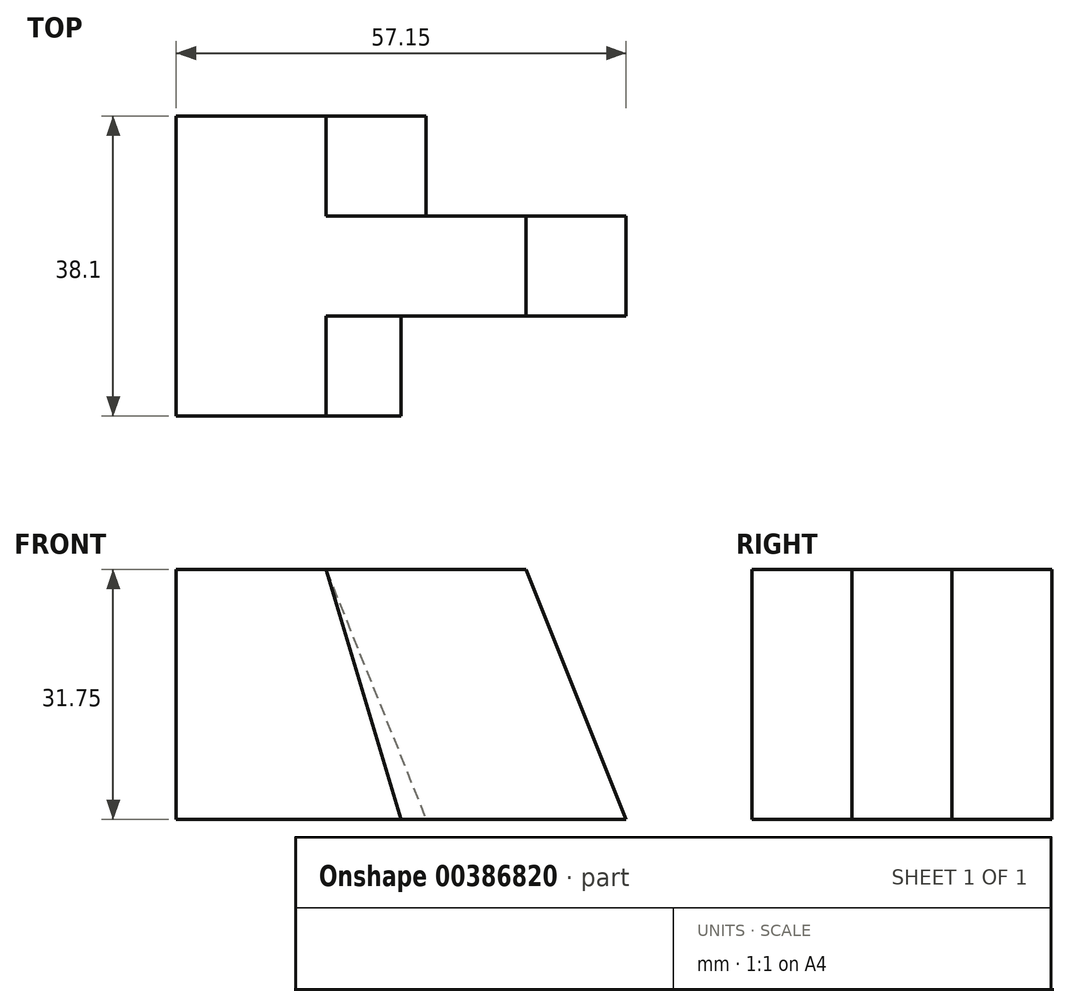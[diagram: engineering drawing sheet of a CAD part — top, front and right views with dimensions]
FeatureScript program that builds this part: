
annotation { "Feature Type Name" : "Feature", "Feature Type Description" : "" }
export const myFeature = defineFeature(function(context is Context, id is Id, definition is map)
    precondition{}
    {
        {
            var Q0;
            Q0=qCreatedBy(makeId("Front.planeOp"),FACE);
            var sketch = newSketch(context, id + "F0", { "sketchPlane" : qUnion([Q0])});
            skLineSegment(sketch, "E0", {"start": v(0, 0) * mm, "end": v(31.75, 0) * mm});
            skLineSegment(sketch, "E1", {"start": v(0, 0) * mm, "end": v(0, 31.75) * mm});
            skLineSegment(sketch, "E2", {"start": v(0, 31.75) * mm, "end": v(19.05, 31.75) * mm});
            skLineSegment(sketch, "E3", {"start": v(19.05, 31.75) * mm, "end": v(31.75, 0) * mm});
            skSolve(sketch);
        }
        {
            var Q0;
            Q0=makeQuery(id+"F0.imprint","IMPRINT",FACE,{"disambiguationData":[TD([[makeQuery(id+"F0.imprint","IMPRINT",EDGE,{"derivedFrom":sQuery(id+"F0.wireOp",EDGE,"E0")}),1.0]])]});
            extrude(context, id + "F1", {"entities" : qUnion([Q0]), "depth" : 25.4 * mm});
        }
        {
            var Q0;
            Q0=makeQuery(id+"F1.opExtrude","CAP_FACE",FACE,{"disambiguationData":[OSD([sQuery(id+"F0.wireOp",EDGE,"E0"),sQuery(id+"F0.wireOp",EDGE,"E1"),sQuery(id+"F0.wireOp",EDGE,"E2"),sQuery(id+"F0.wireOp",EDGE,"E3")])],"isStart":false});
            var sketch = newSketch(context, id + "F2", { "sketchPlane" : qUnion([Q0])});
            skLineSegment(sketch, "E4", {"start": v(31.75, 0) * mm, "end": v(57.15, 0) * mm});
            skLineSegment(sketch, "E5", {"start": v(19.05, 31.75) * mm, "end": v(44.45, 31.75) * mm});
            skLineSegment(sketch, "E6", {"start": v(44.45, 31.75) * mm, "end": v(57.15, 0) * mm});
            skSolve(sketch);
        }
        {
            var Q0;
            Q0=makeQuery(id+"F2.imprint","IMPRINT",FACE,{"disambiguationData":[TD([[makeQuery(id+"F2.imprint","IMPRINT",EDGE,{"derivedFrom":sQuery(id+"F2.wireOp",EDGE,"E4")}),1.0]])]});
            extrude(context, id + "F3", {"entities" : qUnion([Q0]), "operationType" : NewBodyOperationType.ADD, "oppositeDirection" : true, "depth" : 12.7 * mm});
        }
        {
            var Q0;
            {var subQ0=sQuery(id+"F0.wireOp",EDGE,"E3");Q0=makeQuery(id+"F3.boolean.opBoolean","MERGE",FACE,{"derivedFrom":[makeQuery(id+"F1.opExtrude","CAP_FACE",FACE,{"disambiguationData":[OSD([sQuery(id+"F0.wireOp",EDGE,"E0"),sQuery(id+"F0.wireOp",EDGE,"E1"),sQuery(id+"F0.wireOp",EDGE,"E2"),subQ0])],"isStart":false}),makeQuery(id+"F3.opExtrude","CAP_FACE",FACE,{"disambiguationData":[OSD([subQ0,sQuery(id+"F2.wireOp",EDGE,"E4"),sQuery(id+"F2.wireOp",EDGE,"E5"),sQuery(id+"F2.wireOp",EDGE,"E6")])],"isStart":true})]});}
            var sketch = newSketch(context, id + "F4", { "sketchPlane" : qUnion([Q0])});
            skLineSegment(sketch, "E7", {"start": v(0, 0) * mm, "end": v(28.58, 0) * mm});
            skLineSegment(sketch, "E8", {"start": v(0, 31.75) * mm, "end": v(19.05, 31.75) * mm});
            skLineSegment(sketch, "E9", {"start": v(0, 31.75) * mm, "end": v(0, 0) * mm});
            skLineSegment(sketch, "E10", {"start": v(19.05, 31.75) * mm, "end": v(28.57, 0) * mm});
            skSolve(sketch);
        }
        {
            var Q0;
            Q0=makeQuery(id+"F4.imprint","IMPRINT",FACE,{"disambiguationData":[TD([[makeQuery(id+"F4.imprint","IMPRINT",EDGE,{"derivedFrom":sQuery(id+"F4.wireOp",EDGE,"E7")}),1.0]])]});
            extrude(context, id + "F5", {"entities" : qUnion([Q0]), "operationType" : NewBodyOperationType.ADD, "depth" : 12.7 * mm});
        }
    });
